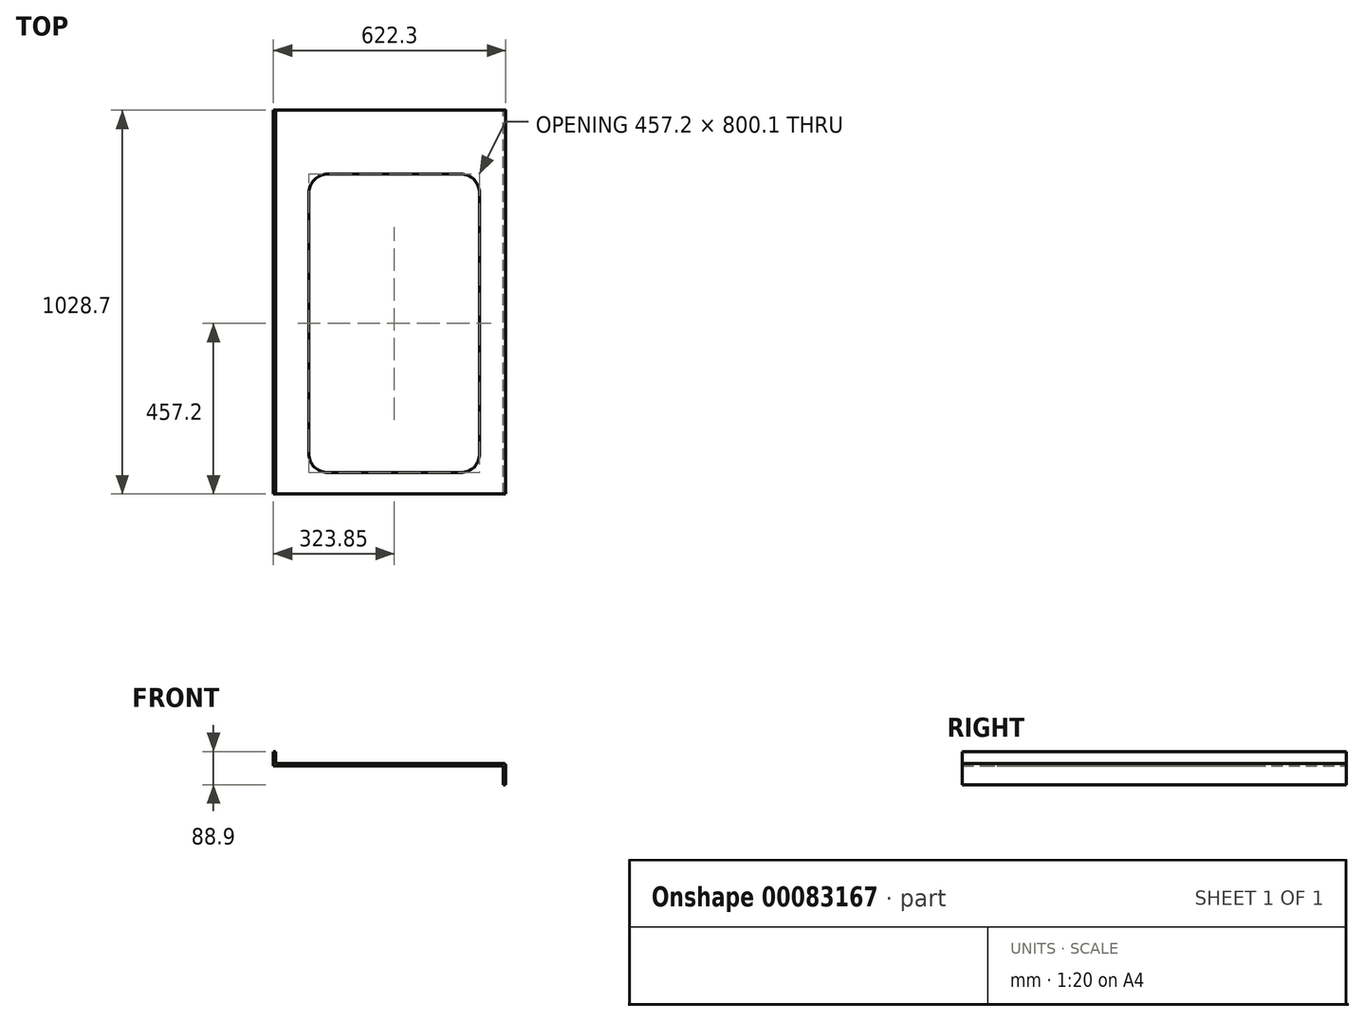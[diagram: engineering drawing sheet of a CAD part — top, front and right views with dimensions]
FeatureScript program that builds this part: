
annotation { "Feature Type Name" : "Feature", "Feature Type Description" : "" }
export const myFeature = defineFeature(function(context is Context, id is Id, definition is map)
    precondition{}
    {
        {
            var Q0;
            Q0=qCreatedBy(makeId("Front.planeOp"),FACE);
            var sketch = newSketch(context, id + "F0", { "sketchPlane" : qUnion([Q0])});
            skLineSegment(sketch, "E0", {"start": v(-609.6, 6.35) * mm, "end": v(0, 6.35) * mm});
            skLineSegment(sketch, "E1", {"start": v(6.35, 0) * mm, "end": v(6.35, -50.8) * mm});
            skLineSegment(sketch, "E2", {"start": v(6.35, -50.8) * mm, "end": v(0, -50.8) * mm});
            skLineSegment(sketch, "E3", {"start": v(0, -50.8) * mm, "end": v(0, 0) * mm});
            skLineSegment(sketch, "E4", {"start": v(0, 0) * mm, "end": v(-615.95, 0) * mm});
            skLineSegment(sketch, "E5", {"start": v(-615.95, 0) * mm, "end": v(-615.95, 38.1) * mm});
            skLineSegment(sketch, "E6", {"start": v(-615.95, 38.1) * mm, "end": v(-609.6, 38.1) * mm});
            skLineSegment(sketch, "E7", {"start": v(-609.6, 38.1) * mm, "end": v(-609.6, 6.35) * mm});
            skPoint(sketch, "E8.visualSharp", {"position": v(6.35, 6.35) * mm});
            skArc(sketch, "E8.filletArc", {"start": v(6.35, 0) * mm, "mid": v(4.5, 4.5) * mm, "end": v(0, 6.35) * mm});
            skSolve(sketch);
        }
        {
            var Q0;
            Q0=makeQuery(id+"F0.imprint","IMPRINT",FACE,{"disambiguationData":[TD([[makeQuery(id+"F0.imprint","IMPRINT",EDGE,{"derivedFrom":sQuery(id+"F0.wireOp",EDGE,"E0")}),-1.0]])]});
            extrude(context, id + "F1", {"entities" : qUnion([Q0]), "depth" : 1028.7 * mm, "symmetric" : true});
        }
        {
            var Q0;
            Q0=makeQuery(id+"F1.opExtrude","SWEPT_FACE",FACE,{"disambiguationData":[OSD([sQuery(id+"F0.wireOp",EDGE,"E0")])]});
            var sketch = newSketch(context, id + "F2", { "sketchPlane" : qUnion([Q0])});
            skLineSegment(sketch, "E9.bottom", {"start": v(-469.9, 342.9) * mm, "end": v(-114.3, 342.9) * mm});
            skLineSegment(sketch, "E9.top", {"start": v(-469.9, -457.2) * mm, "end": v(-114.3, -457.2) * mm});
            skLineSegment(sketch, "E9.left", {"start": v(-520.7, 292.1) * mm, "end": v(-520.7, -406.4) * mm});
            skLineSegment(sketch, "E9.right", {"start": v(-63.5, 292.1) * mm, "end": v(-63.5, -406.4) * mm});
            skPoint(sketch, "E9.middle", {"position": v(-292.1, 0) * mm});
            skPoint(sketch, "E9.middle.positionSnap0", {"position": v(0, 0) * mm});
            skPoint(sketch, "E9.centerSnap0", {"position": v(0, 0) * mm});
            skPoint(sketch, "E10.visualSharp", {"position": v(-520.7, -457.2) * mm});
            skArc(sketch, "E10.filletArc", {"start": v(-520.7, -406.4) * mm, "mid": v(-505.82, -442.32) * mm, "end": v(-469.9, -457.2) * mm});
            skPoint(sketch, "E11.visualSharp", {"position": v(-520.7, 342.9) * mm});
            skArc(sketch, "E11.filletArc", {"start": v(-469.9, 342.9) * mm, "mid": v(-505.82, 328.02) * mm, "end": v(-520.7, 292.1) * mm});
            skPoint(sketch, "E12.visualSharp", {"position": v(-63.5, 342.9) * mm});
            skArc(sketch, "E12.filletArc", {"start": v(-63.5, 292.1) * mm, "mid": v(-78.38, 328.02) * mm, "end": v(-114.3, 342.9) * mm});
            skPoint(sketch, "E13.visualSharp", {"position": v(-63.5, -457.2) * mm});
            skArc(sketch, "E13.filletArc", {"start": v(-114.3, -457.2) * mm, "mid": v(-78.38, -442.32) * mm, "end": v(-63.5, -406.4) * mm});
            skSolve(sketch);
        }
        {
            var Q0;
            Q0=makeQuery(id+"F2.imprint","IMPRINT",FACE,{"disambiguationData":[TD([[makeQuery(id+"F2.imprint","IMPRINT",EDGE,{"derivedFrom":sQuery(id+"F2.wireOp",EDGE,"E9.bottom")}),-1.0]])]});
            extrude(context, id + "F3", {"entities" : qUnion([Q0]), "operationType" : NewBodyOperationType.REMOVE, "oppositeDirection" : true, "depth" : 25.4 * mm});
        }
    });
